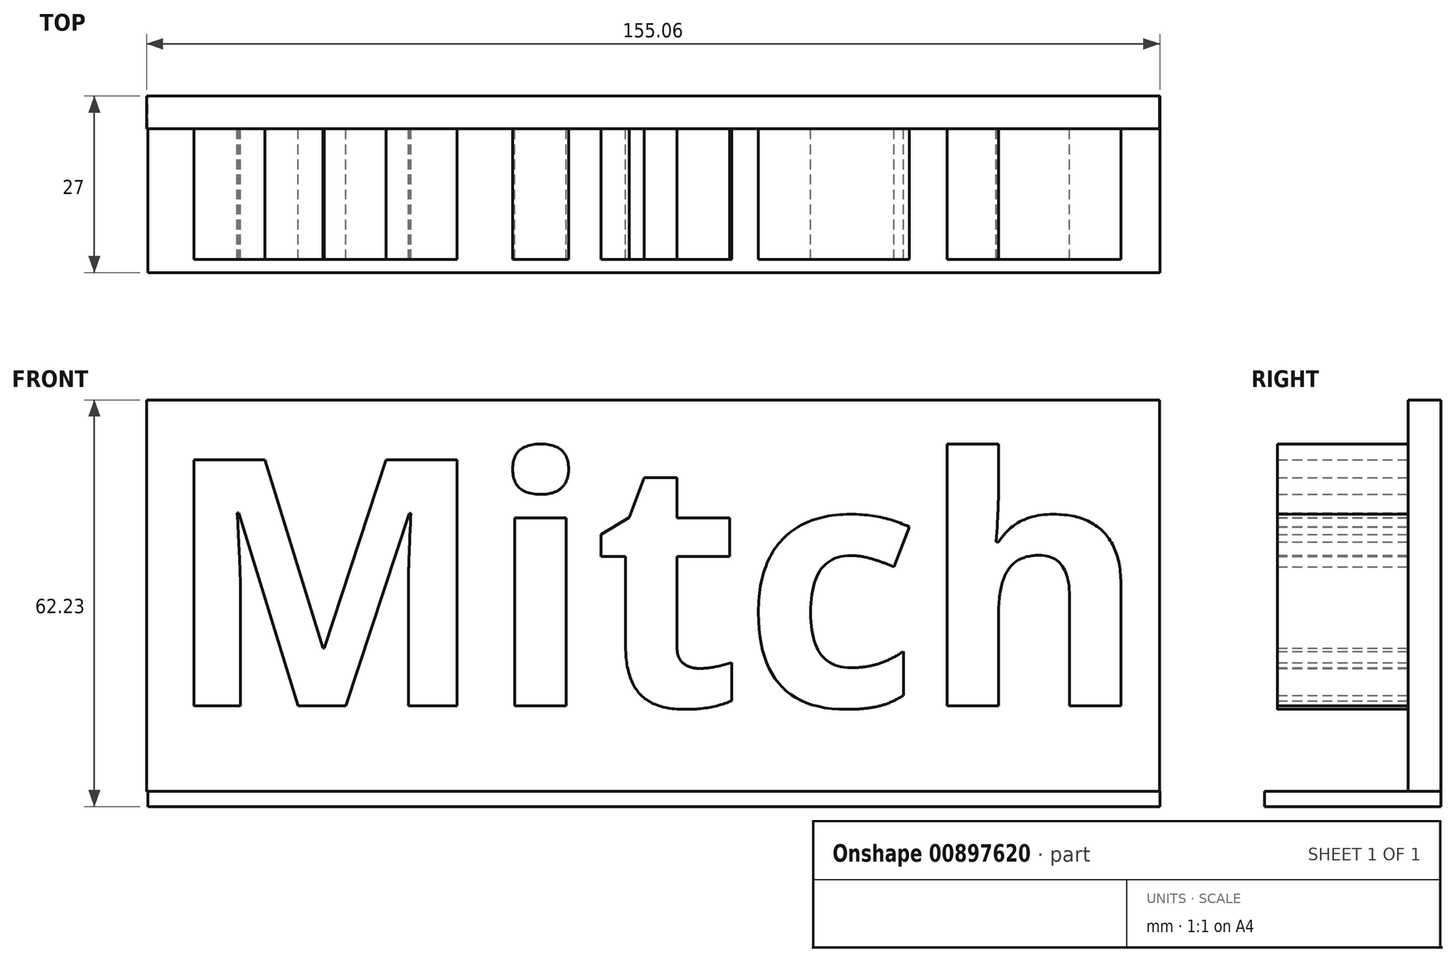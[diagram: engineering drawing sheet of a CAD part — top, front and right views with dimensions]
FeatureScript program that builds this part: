
annotation { "Feature Type Name" : "Feature", "Feature Type Description" : "" }
export const myFeature = defineFeature(function(context is Context, id is Id, definition is map)
    precondition{}
    {
        {
            var Q0;
            Q0=qCreatedBy(makeId("Front.planeOp"),FACE);
            var sketch = newSketch(context, id + "F0", { "sketchPlane" : qUnion([Q0])});
            skText(sketch, "E0", { "text": "Mitch", "fontName": "OpenSans-Bold.ttf"});
            const initialGuessF0  = {"E0": [-0.075, 0.0305, 1, 0, 0.03799]};
            skSetInitialGuess(sketch, initialGuessF0);
            skSolve(sketch);
        }
        {
            var Q0;
            Q0 = qSketchRegion(id + "F0", true);
            extrude(context, id + "F1", {"entities" : qUnion([Q0]), "depth" : 25 * mm, "offsetDistance" : 25.4 * mm});
        }
        {
            var Q0;
            Q0=qCreatedBy(makeId("Front.planeOp"),FACE);
            var sketch = newSketch(context, id + "F2", { "sketchPlane" : qUnion([Q0])});
            skLineSegment(sketch, "E1.bottom", {"start": v(-77.5, 77.34) * mm, "end": v(77.5, 77.34) * mm});
            skLineSegment(sketch, "E1.top", {"start": v(-77.5, 17.34) * mm, "end": v(77.5, 17.34) * mm});
            skLineSegment(sketch, "E1.left", {"start": v(-77.5, 77.34) * mm, "end": v(-77.5, 17.34) * mm});
            skLineSegment(sketch, "E1.right", {"start": v(77.5, 77.34) * mm, "end": v(77.5, 17.34) * mm});
            skSolve(sketch);
        }
        {
            var Q0;
            Q0=makeQuery(id+"F2.imprint","IMPRINT",FACE,{"disambiguationData":[TD([[makeQuery(id+"F2.imprint","IMPRINT",EDGE,{"derivedFrom":sQuery(id+"F2.wireOp",EDGE,"E1.bottom")}),-1.0]])]});
            extrude(context, id + "F3", {"entities" : qUnion([Q0]), "operationType" : NewBodyOperationType.ADD, "depth" : 5 * mm, "offsetDistance" : 25.4 * mm});
        }
        {
            var Q0;
            Q0=qCreatedBy(makeId("Front.planeOp"),FACE);
            var sketch = newSketch(context, id + "F4", { "sketchPlane" : qUnion([Q0])});
            skLineSegment(sketch, "E2.bottom", {"start": v(-77.28, 17.41) * mm, "end": v(77.56, 17.41) * mm});
            skLineSegment(sketch, "E2.top", {"start": v(-77.28, 15.1) * mm, "end": v(77.56, 15.1) * mm});
            skLineSegment(sketch, "E2.left", {"start": v(-77.28, 17.41) * mm, "end": v(-77.28, 15.1) * mm});
            skLineSegment(sketch, "E2.right", {"start": v(77.56, 17.41) * mm, "end": v(77.56, 15.1) * mm});
            skSolve(sketch);
        }
        {
            var Q0;
            Q0=makeQuery(id+"F4.imprint","IMPRINT",FACE,{"disambiguationData":[TD([[makeQuery(id+"F4.imprint","IMPRINT",EDGE,{"derivedFrom":sQuery(id+"F4.wireOp",EDGE,"E2.bottom")}),-1.0]])]});
            extrude(context, id + "F5", {"entities" : qUnion([Q0]), "operationType" : NewBodyOperationType.ADD, "depth" : 27 * mm, "offsetDistance" : 25.4 * mm});
        }
    });
